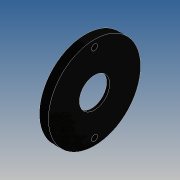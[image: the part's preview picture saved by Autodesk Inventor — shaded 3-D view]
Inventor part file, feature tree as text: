
AUTODESK INVENTOR PART (.ipt)
format: ipt  version: 2015 SP1 (Build 190203100, 203)  size: 209,408 bytes
history: native  units: mm
features: sketch x2, revolve x1, hole x1, mirror x1
ambient origin geometry x8: Origin, YZ Plane, XZ Plane, XY Plane, X Axis, Y Axis, Z Axis, Center Point
bodies: Solid1 (feature_tree)
feature tree (5):
  revolve  "Revolution1"  [1 undecoded]
  hole  "Hole1"  [1 undecoded]
  mirror  "Mirror1"
  sketch  "Sketch1"  dims[d0=30.5mm d1=10.0mm]
  sketch  "Sketch2"  dims[d2=22.0mm d3=1.0mm d4=3.0mm d5=90.0deg d6=13.0mm d7=2.0mm d8=6.0mm d9=4.0mm d10=2.0mm d11=90.0deg d12=8.0mm d13=20.594885mm]
note: 2 required parameter values undecoded (feature->parameter linkage not recoverable at this tier; creation-order binding heuristic only, values carry confidence <= 0.55)